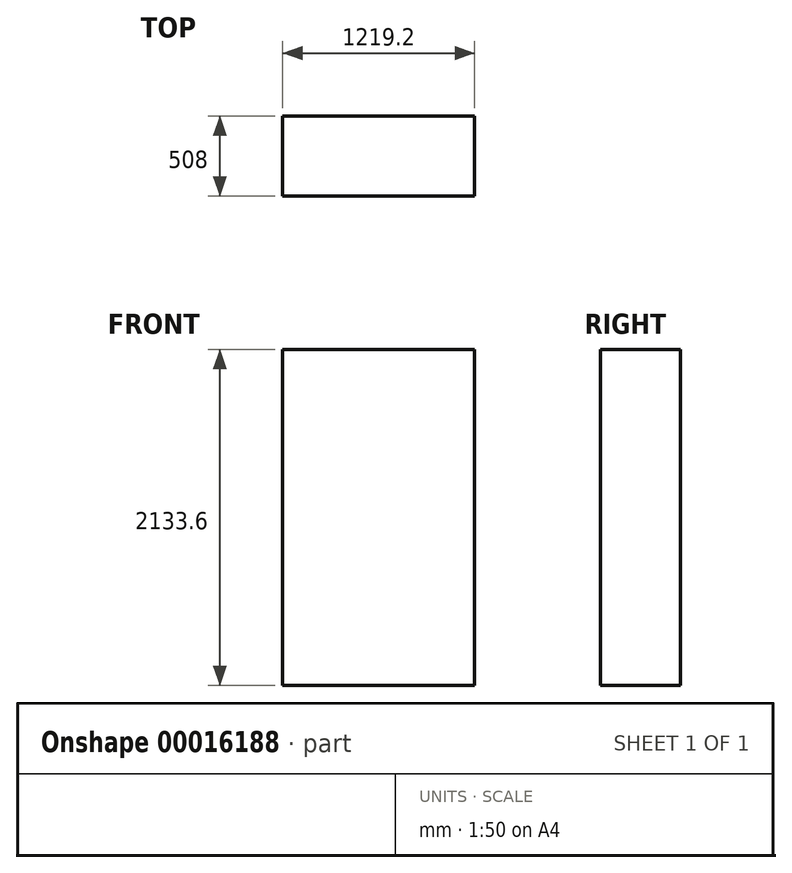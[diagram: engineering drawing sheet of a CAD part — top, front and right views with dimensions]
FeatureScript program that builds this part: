
annotation { "Feature Type Name" : "Feature", "Feature Type Description" : "" }
export const myFeature = defineFeature(function(context is Context, id is Id, definition is map)
    precondition{}
    {
        {
            var Q0;
            Q0=qCreatedBy(makeId("Top.planeOp"),FACE);
            var sketch = newSketch(context, id + "F0", { "sketchPlane" : qUnion([Q0])});
            skLineSegment(sketch, "E0.rect.bottom", {"start": v(609.6, -254) * mm, "end": v(-609.6, -254) * mm});
            skLineSegment(sketch, "E0.rect.top", {"start": v(609.6, 254) * mm, "end": v(-609.6, 254) * mm});
            skLineSegment(sketch, "E0.rect.left", {"start": v(609.6, -254) * mm, "end": v(609.6, 254) * mm});
            skLineSegment(sketch, "E0.rect.right", {"start": v(-609.6, -254) * mm, "end": v(-609.6, 254) * mm});
            skPoint(sketch, "E0.rect.middle", {"position": v(0, 0) * mm});
            skSolve(sketch);
        }
        {
            var Q0;
            Q0 = qSketchRegion(id + "F0", true);
            extrude(context, id + "F1", {"entities" : qUnion([Q0]), "depth" : 7 * 304.8 * mm});
        }
    });
